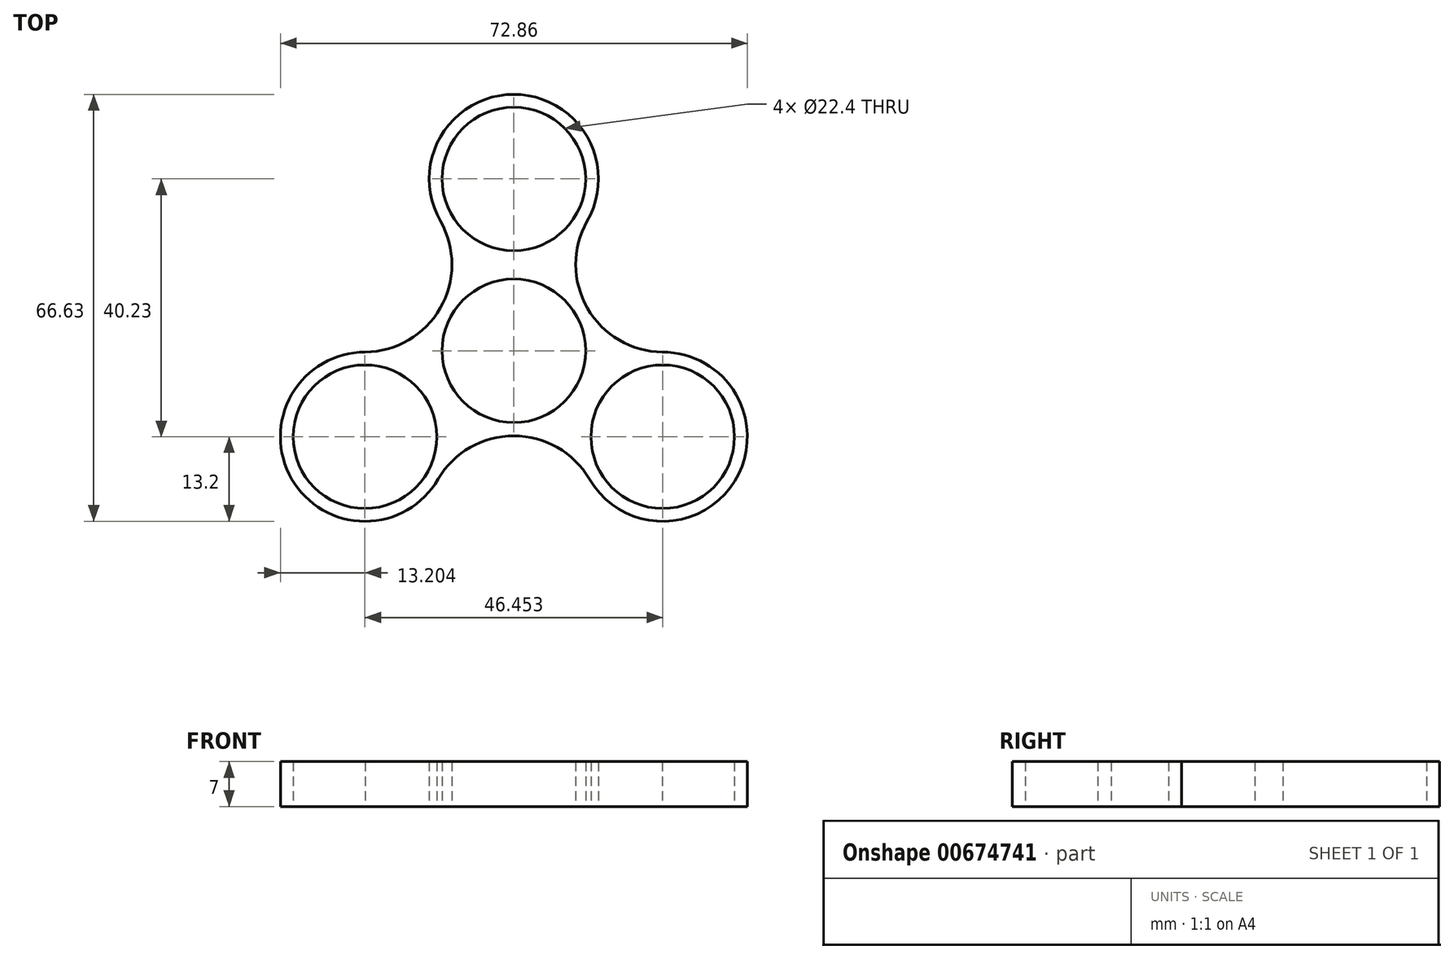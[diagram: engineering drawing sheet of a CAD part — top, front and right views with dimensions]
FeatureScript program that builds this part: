
annotation { "Feature Type Name" : "Feature", "Feature Type Description" : "" }
export const myFeature = defineFeature(function(context is Context, id is Id, definition is map)
    precondition{}
    {
        {
            var Q0;
            Q0=qCreatedBy(makeId("Top.planeOp"),FACE);
            var sketch = newSketch(context, id + "F0", { "sketchPlane" : qUnion([Q0])});
            skCircle(sketch, "E0", {"center": v(0, 0) * mm, "radius": 11.2 * mm});
            skCircle(sketch, "E1", {"center": v(0, 26.82) * mm, "radius": 11.2 * mm});
            skArc(sketch, "E2", {"start": v(11.43, 20.22) * mm, "mid": v(0, 40.02) * mm, "end": v(-11.43, 20.22) * mm});
            skCircle(sketch, "E3.1.0", {"center": v(-23.23, -13.41) * mm, "radius": 11.2 * mm});
            skArc(sketch, "E3.1.1", {"start": v(-23.18, -0.21) * mm, "mid": v(-34.67, -20) * mm, "end": v(-11.8, -20.01) * mm});
            skCircle(sketch, "E3.2.0", {"center": v(23.23, -13.4) * mm, "radius": 11.2 * mm});
            skArc(sketch, "E3.2.1", {"start": v(11.8, -20.01) * mm, "mid": v(34.67, -20) * mm, "end": v(23.19, -0.2) * mm});
            skArc(sketch, "E4.2.0", {"start": v(-23.23, -0.21) * mm, "mid": v(-34.66, -20.01) * mm, "end": v(-11.8, -20.01) * mm});
            skArc(sketch, "E4.4.0", {"start": v(11.8, -20.01) * mm, "mid": v(34.66, -20.01) * mm, "end": v(23.23, -0.21) * mm});
            skArc(sketch, "E5", {"start": v(11.43, 20.22) * mm, "mid": v(11.5, 6.63) * mm, "end": v(23.23, -0.21) * mm});
            skArc(sketch, "E6.1.0", {"start": v(-23.18, -0.21) * mm, "mid": v(-11.48, 6.65) * mm, "end": v(-11.43, 20.22) * mm});
            skArc(sketch, "E6.2.0", {"start": v(11.8, -20.01) * mm, "mid": v(0, -13.27) * mm, "end": v(-11.8, -20.01) * mm});
            skSolve(sketch);
        }
        {
            var Q0;
            Q0 = qSketchRegion(id + "F0", true);
            extrude(context, id + "F1", {"entities" : qUnion([Q0]), "depth" : 7 * mm, "offsetDistance" : 25 * mm});
        }
    });
